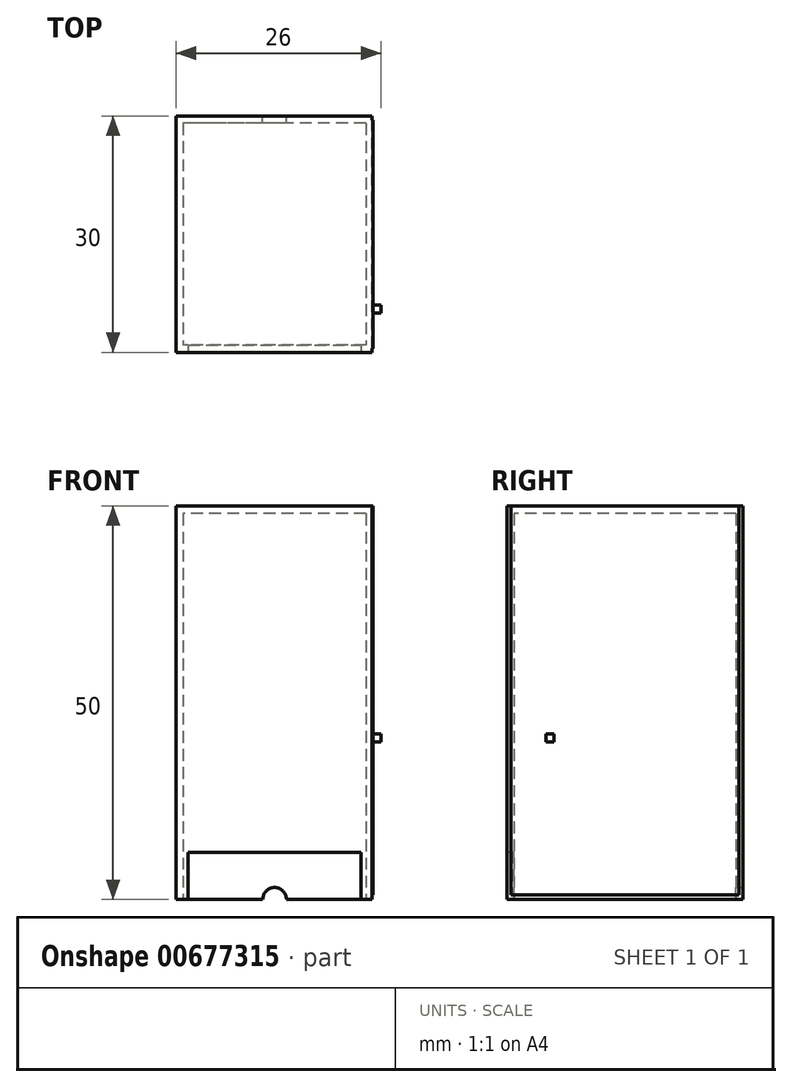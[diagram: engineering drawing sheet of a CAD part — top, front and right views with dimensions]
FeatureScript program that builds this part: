
annotation { "Feature Type Name" : "Feature", "Feature Type Description" : "" }
export const myFeature = defineFeature(function(context is Context, id is Id, definition is map)
    precondition{}
    {
        {
            var Q0;
            Q0=qCreatedBy(makeId("Top.planeOp"),FACE);
            var sketch = newSketch(context, id + "F0", { "sketchPlane" : qUnion([Q0])});
            skLineSegment(sketch, "E0.bottom", {"start": v(12.5, 15) * mm, "end": v(-12.5, 15) * mm});
            skLineSegment(sketch, "E0.top", {"start": v(12.5, -15) * mm, "end": v(-12.5, -15) * mm});
            skLineSegment(sketch, "E0.left", {"start": v(12.5, 15) * mm, "end": v(12.5, -15) * mm});
            skLineSegment(sketch, "E0.right", {"start": v(-12.5, 15) * mm, "end": v(-12.5, -15) * mm});
            skPoint(sketch, "E0.middle", {"position": v(0, 0) * mm});
            skLineSegment(sketch, "E1.0", {"start": v(11.6, 14.1) * mm, "end": v(-11.6, 14.1) * mm});
            skLineSegment(sketch, "E1.1", {"start": v(11.6, 14.1) * mm, "end": v(11.6, -14.1) * mm});
            skLineSegment(sketch, "E1.2", {"start": v(11.6, -14.1) * mm, "end": v(-11.6, -14.1) * mm});
            skLineSegment(sketch, "E1.3", {"start": v(-11.6, 14.1) * mm, "end": v(-11.6, -14.1) * mm});
            skSolve(sketch);
        }
        {
            var Q0;
            Q0 = qSketchRegion(id + "F0", true);
            extrude(context, id + "F1", {"entities" : qUnion([Q0]), "depth" : 50 * mm, "offsetDistance" : 25 * mm});
        }
        {
            var Q0;
            Q0=makeQuery(id+"F1.opExtrude","CAP_FACE",FACE,{"disambiguationData":[OSD([sQuery(id+"F0.wireOp",EDGE,"E0.bottom"),sQuery(id+"F0.wireOp",EDGE,"E0.top"),sQuery(id+"F0.wireOp",EDGE,"E0.left"),sQuery(id+"F0.wireOp",EDGE,"E0.right"),sQuery(id+"F0.wireOp",EDGE,"E1.0"),sQuery(id+"F0.wireOp",EDGE,"E1.1"),sQuery(id+"F0.wireOp",EDGE,"E1.2"),sQuery(id+"F0.wireOp",EDGE,"E1.3")])],"isStart":false});
            var sketch = newSketch(context, id + "F2", { "sketchPlane" : qUnion([Q0])});
            skLineSegment(sketch, "E2.bottom", {"start": v(12.5, -15) * mm, "end": v(-12.5, -15) * mm});
            skLineSegment(sketch, "E2.top", {"start": v(12.5, 15) * mm, "end": v(-12.5, 15) * mm});
            skLineSegment(sketch, "E2.left", {"start": v(12.5, -15) * mm, "end": v(12.5, 15) * mm});
            skLineSegment(sketch, "E2.right", {"start": v(-12.5, -15) * mm, "end": v(-12.5, 15) * mm});
            skPoint(sketch, "E2.middle", {"position": v(0, 0) * mm});
            skSolve(sketch);
        }
        {
            var Q0;
            Q0 = qSketchRegion(id + "F2", true);
            extrude(context, id + "F3", {"entities" : qUnion([Q0]), "operationType" : NewBodyOperationType.ADD, "oppositeDirection" : true, "depth" : 1 * mm, "offsetDistance" : 25 * mm});
        }
        {
            var Q0;
            Q0=makeQuery(id+"F1.opExtrude","SWEPT_FACE",FACE,{"disambiguationData":[OSD([sQuery(id+"F0.wireOp",EDGE,"E0.left")])]});
            var sketch = newSketch(context, id + "F4", { "sketchPlane" : qUnion([Q0])});
            skLineSegment(sketch, "E3.bottom", {"start": v(-9, 20) * mm, "end": v(-10, 20) * mm});
            skLineSegment(sketch, "E3.top", {"start": v(-9, 21) * mm, "end": v(-10, 21) * mm});
            skLineSegment(sketch, "E3.left", {"start": v(-9, 20) * mm, "end": v(-9, 21) * mm});
            skLineSegment(sketch, "E3.right", {"start": v(-10, 20) * mm, "end": v(-10, 21) * mm});
            skPoint(sketch, "E3.middle", {"position": v(-9.5, 20.5) * mm});
            skSolve(sketch);
        }
        {
            var Q0;
            Q0 = qSketchRegion(id + "F4", true);
            extrude(context, id + "F5", {"entities" : qUnion([Q0]), "operationType" : NewBodyOperationType.ADD, "depth" : 1 * mm, "offsetDistance" : 25 * mm});
        }
        {
            var Q0;
            Q0=makeQuery(id+"F1.opExtrude","SWEPT_FACE",FACE,{"disambiguationData":[OSD([sQuery(id+"F0.wireOp",EDGE,"E0.top")])]});
            var sketch = newSketch(context, id + "F6", { "sketchPlane" : qUnion([Q0])});
            skLineSegment(sketch, "E4.bottom", {"start": v(-11, 0) * mm, "end": v(11, 0) * mm});
            skLineSegment(sketch, "E4.top", {"start": v(-11, 6) * mm, "end": v(11, 6) * mm});
            skLineSegment(sketch, "E4.left", {"start": v(-11, 0) * mm, "end": v(-11, 6) * mm});
            skLineSegment(sketch, "E4.right", {"start": v(11, 0) * mm, "end": v(11, 6) * mm});
            skSolve(sketch);
        }
        {
            var Q0;
            Q0 = qSketchRegion(id + "F6", true);
            extrude(context, id + "F7", {"entities" : qUnion([Q0]), "operationType" : NewBodyOperationType.REMOVE, "oppositeDirection" : true, "depth" : 10 * mm, "offsetDistance" : 25 * mm});
        }
        {
            var Q0;
            Q0=makeQuery(id+"F1.opExtrude","SWEPT_FACE",FACE,{"disambiguationData":[OSD([sQuery(id+"F0.wireOp",EDGE,"E0.bottom")])]});
            var sketch = newSketch(context, id + "F8", { "sketchPlane" : qUnion([Q0])});
            skCircle(sketch, "E5", {"center": v(0, 0) * mm, "radius": 1.5 * mm});
            skSolve(sketch);
        }
        {
            var Q0;
            Q0 = qSketchRegion(id + "F8", true);
            extrude(context, id + "F9", {"entities" : qUnion([Q0]), "operationType" : NewBodyOperationType.REMOVE, "oppositeDirection" : true, "depth" : 5 * mm, "offsetDistance" : 25 * mm});
        }
        {
            var Q0;
            Q0=makeQuery(id+"F1.opExtrude","SWEPT_FACE",FACE,{"disambiguationData":[OSD([sQuery(id+"F0.wireOp",EDGE,"E0.left")])]});
            var sketch = newSketch(context, id + "F10", { "sketchPlane" : qUnion([Q0])});
            skLineSegment(sketch, "E6.bottom", {"start": v(-14.5, 0.6) * mm, "end": v(14.5, 0.6) * mm});
            skLineSegment(sketch, "E6.top", {"start": v(-14.5, 50) * mm, "end": v(14.5, 50) * mm});
            skLineSegment(sketch, "E6.left", {"start": v(-14.5, 0.6) * mm, "end": v(-14.5, 50) * mm});
            skLineSegment(sketch, "E6.right", {"start": v(14.5, 0.6) * mm, "end": v(14.5, 50) * mm});
            skSolve(sketch);
        }
        {
            var Q0;
            Q0=makeQuery(id+"F10.imprint","IMPRINT",FACE,{"disambiguationData":[TD([[makeQuery(id+"F10.imprint","IMPRINT",EDGE,{"derivedFrom":sQuery(id+"F10.wireOp",EDGE,"E6.bottom")}),-1.0]])]});
            extrude(context, id + "F11", {"entities" : qUnion([Q0]), "operationType" : NewBodyOperationType.REMOVE, "oppositeDirection" : true, "depth" : 0.1 * mm, "offsetDistance" : 25 * mm});
        }
    });
